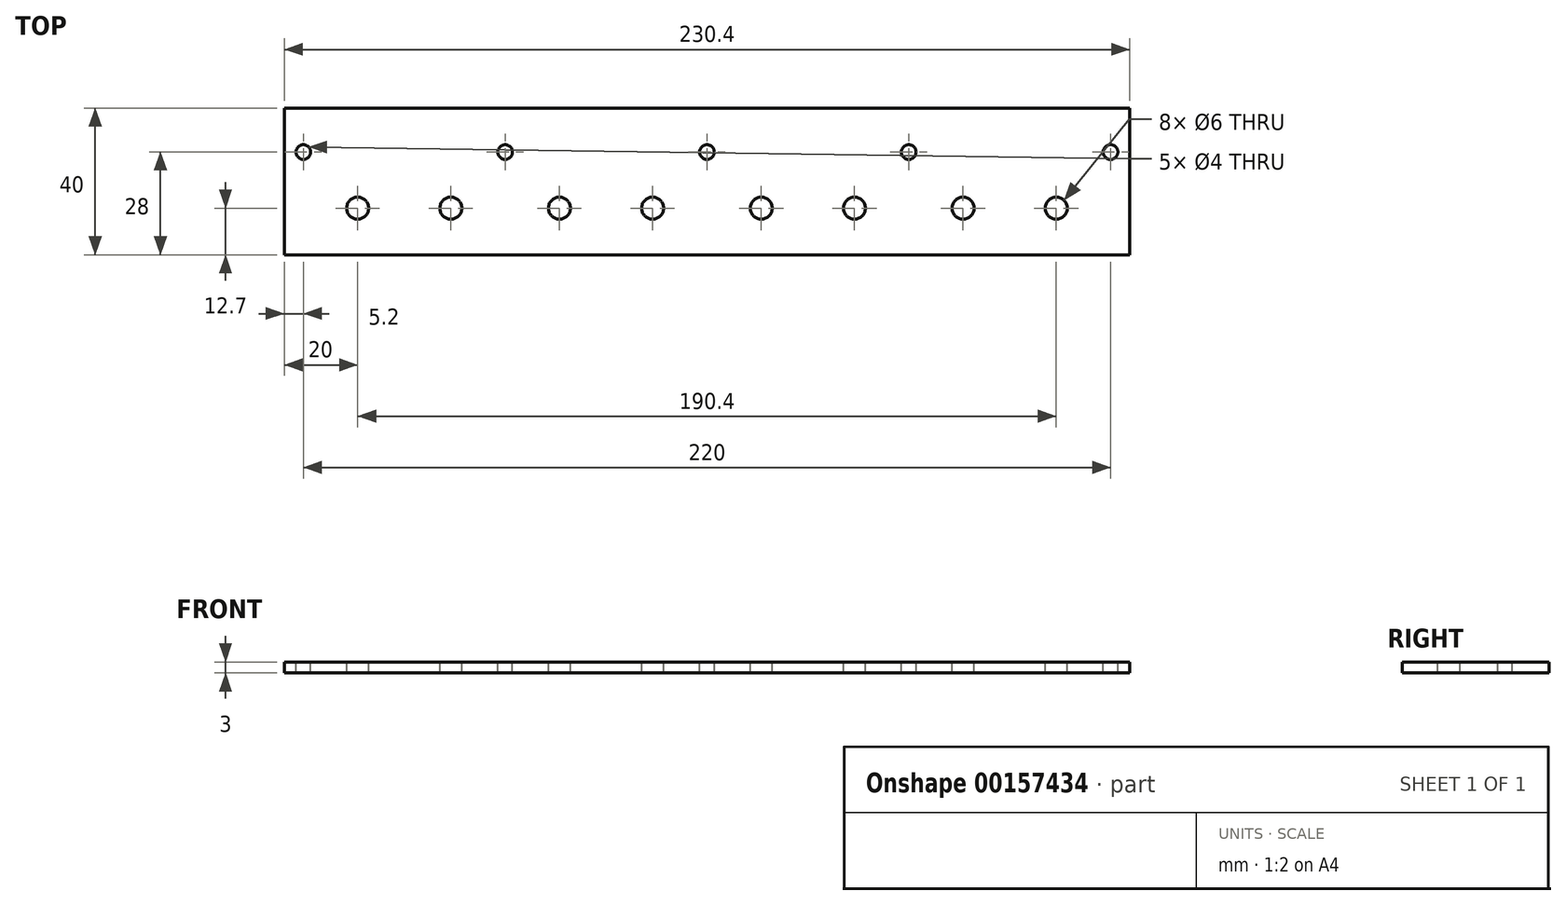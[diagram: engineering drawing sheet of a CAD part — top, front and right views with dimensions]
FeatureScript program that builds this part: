
annotation { "Feature Type Name" : "Feature", "Feature Type Description" : "" }
export const myFeature = defineFeature(function(context is Context, id is Id, definition is map)
    precondition{}
    {
        {
            var Q0;
            Q0=qCreatedBy(makeId("Top.planeOp"),FACE);
            var sketch = newSketch(context, id + "F0", { "sketchPlane" : qUnion([Q0])});
            skLineSegment(sketch, "E0.bottom", {"start": v(0, 0) * mm, "end": v(230.4, 0) * mm});
            skLineSegment(sketch, "E0.top", {"start": v(0, 40) * mm, "end": v(230.4, 40) * mm});
            skLineSegment(sketch, "E0.left", {"start": v(0, 0) * mm, "end": v(0, 40) * mm});
            skLineSegment(sketch, "E0.right", {"start": v(230.4, 0) * mm, "end": v(230.4, 40) * mm});
            skSolve(sketch);
        }
        {
            var Q0;
            Q0=qSketchRegion(id+"F0",true);
            extrude(context, id + "F1", {"entities" : qUnion([Q0]), "depth" : 3 * mm});
        }
        {
            var Q0;
            Q0=makeQuery(id+"F1.opExtrude","CAP_FACE",FACE,{"disambiguationData":[OSD([sQuery(id+"F0.wireOp",EDGE,"E0.bottom"),sQuery(id+"F0.wireOp",EDGE,"E0.top"),sQuery(id+"F0.wireOp",EDGE,"E0.left"),sQuery(id+"F0.wireOp",EDGE,"E0.right")])],"isStart":false});
            var sketch = newSketch(context, id + "F2", { "sketchPlane" : qUnion([Q0])});
            skCircle(sketch, "E1", {"center": v(5.2, 28) * mm, "radius": 2 * mm});
            skCircle(sketch, "E2.1.0.0", {"center": v(60.2, 28) * mm, "radius": 2 * mm});
            skCircle(sketch, "E2.2.0.0", {"center": v(115.2, 28) * mm, "radius": 2 * mm});
            skCircle(sketch, "E2.3.0.0", {"center": v(170.2, 28) * mm, "radius": 2 * mm});
            skCircle(sketch, "E2.4.0.0", {"center": v(225.2, 28) * mm, "radius": 2 * mm});
            skLineSegment(sketch, "E2.direction1", {"start": v(5.2, 28) * mm, "end": v(60.2, 28) * mm, "construction": true});
            skSolve(sketch);
        }
        {
            var Q0;
            Q0=qSketchRegion(id+"F2",true);
            extrude(context, id + "F3", {"entities" : qUnion([Q0]), "operationType" : NewBodyOperationType.REMOVE, "endBound" : BoundingType.THROUGH_ALL, "oppositeDirection" : true, "depth" : 25 * mm});
        }
        {
            var Q0;
            Q0=makeQuery(id+"F1.opExtrude","CAP_FACE",FACE,{"disambiguationData":[OSD([sQuery(id+"F0.wireOp",EDGE,"E0.bottom"),sQuery(id+"F0.wireOp",EDGE,"E0.top"),sQuery(id+"F0.wireOp",EDGE,"E0.left"),sQuery(id+"F0.wireOp",EDGE,"E0.right")])],"isStart":false});
            var sketch = newSketch(context, id + "F4", { "sketchPlane" : qUnion([Q0])});
            skCircle(sketch, "E3", {"center": v(20, 12.7) * mm, "radius": 3 * mm});
            skCircle(sketch, "E4", {"center": v(45.4, 12.7) * mm, "radius": 3 * mm});
            skCircle(sketch, "E5.1.0.0", {"center": v(75, 12.7) * mm, "radius": 3 * mm});
            skCircle(sketch, "E5.1.0.1", {"center": v(100.4, 12.7) * mm, "radius": 3 * mm});
            skCircle(sketch, "E5.2.0.0", {"center": v(130, 12.7) * mm, "radius": 3 * mm});
            skCircle(sketch, "E5.2.0.1", {"center": v(155.4, 12.7) * mm, "radius": 3 * mm});
            skCircle(sketch, "E5.3.0.0", {"center": v(185, 12.7) * mm, "radius": 3 * mm});
            skCircle(sketch, "E5.3.0.1", {"center": v(210.4, 12.7) * mm, "radius": 3 * mm});
            skLineSegment(sketch, "E5.direction1", {"start": v(20, 12.7) * mm, "end": v(75, 12.7) * mm, "construction": true});
            skSolve(sketch);
        }
        {
            var Q0;
            Q0 = qSketchRegion(id + "F4", true);
            extrude(context, id + "F5", {"entities" : qUnion([Q0]), "operationType" : NewBodyOperationType.REMOVE, "endBound" : BoundingType.THROUGH_ALL, "oppositeDirection" : true, "depth" : 25 * mm});
        }
    });
